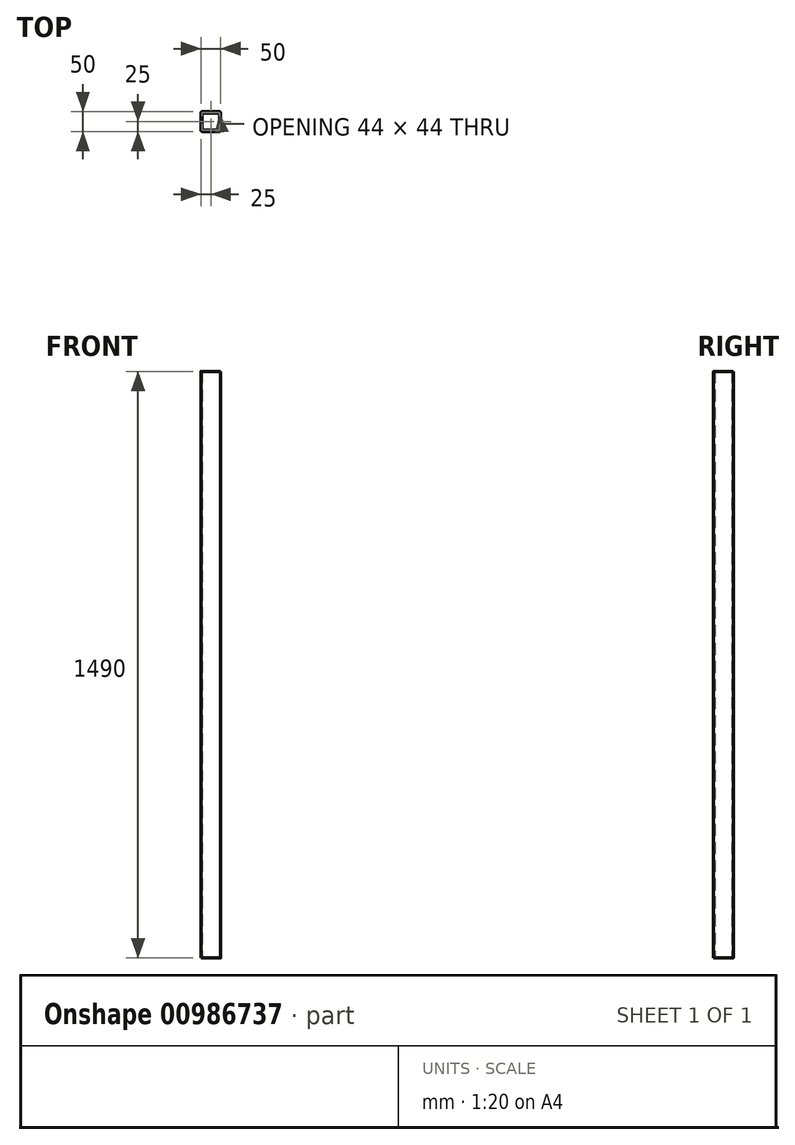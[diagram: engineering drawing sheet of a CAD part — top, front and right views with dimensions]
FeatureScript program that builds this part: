
annotation { "Feature Type Name" : "Feature", "Feature Type Description" : "" }
export const myFeature = defineFeature(function(context is Context, id is Id, definition is map)
    precondition{}
    {
        {
            var Q0;
            Q0=qCreatedBy(makeId("Top.planeOp"),FACE);
            var sketch = newSketch(context, id + "F0", { "sketchPlane" : qUnion([Q0])});
            skLineSegment(sketch, "E0.bottom", {"start": v(22, -25) * mm, "end": v(-22, -25) * mm});
            skLineSegment(sketch, "E0.top", {"start": v(22, 25) * mm, "end": v(-22, 25) * mm});
            skLineSegment(sketch, "E0.left", {"start": v(25, -22) * mm, "end": v(25, 22) * mm});
            skLineSegment(sketch, "E0.right", {"start": v(-25, -22) * mm, "end": v(-25, 22) * mm});
            skPoint(sketch, "E0.middle", {"position": v(0, 0) * mm});
            skLineSegment(sketch, "E1.0", {"start": v(-22, -19) * mm, "end": v(-22, 19) * mm});
            skLineSegment(sketch, "E1.1", {"start": v(19, -22) * mm, "end": v(-19, -22) * mm});
            skLineSegment(sketch, "E1.2", {"start": v(22, -19) * mm, "end": v(22, 19) * mm});
            skLineSegment(sketch, "E1.3", {"start": v(19, 22) * mm, "end": v(-19, 22) * mm});
            skPoint(sketch, "E2.visualSharp", {"position": v(-25, 25) * mm});
            skArc(sketch, "E2.filletArc", {"start": v(-22, 25) * mm, "mid": v(-24.12, 24.12) * mm, "end": v(-25, 22) * mm});
            skPoint(sketch, "E3.visualSharp", {"position": v(25, 25) * mm});
            skArc(sketch, "E3.filletArc", {"start": v(25, 22) * mm, "mid": v(24.12, 24.12) * mm, "end": v(22, 25) * mm});
            skPoint(sketch, "E4.visualSharp", {"position": v(25, -25) * mm});
            skArc(sketch, "E4.filletArc", {"start": v(22, -25) * mm, "mid": v(24.12, -24.12) * mm, "end": v(25, -22) * mm});
            skPoint(sketch, "E5.visualSharp", {"position": v(-25, -25) * mm});
            skArc(sketch, "E5.filletArc", {"start": v(-25, -22) * mm, "mid": v(-24.12, -24.12) * mm, "end": v(-22, -25) * mm});
            skArc(sketch, "E6.filletArc", {"start": v(22, 19) * mm, "mid": v(21.12, 21.12) * mm, "end": v(19, 22) * mm});
            skArc(sketch, "E7.filletArc", {"start": v(-19, 22) * mm, "mid": v(-21.12, 21.12) * mm, "end": v(-22, 19) * mm});
            skArc(sketch, "E8.filletArc", {"start": v(-22, -19) * mm, "mid": v(-21.12, -21.12) * mm, "end": v(-19, -22) * mm});
            skArc(sketch, "E9.filletArc", {"start": v(19, -22) * mm, "mid": v(21.12, -21.12) * mm, "end": v(22, -19) * mm});
            skSolve(sketch);
        }
        {
            var Q0;
            Q0 = qSketchRegion(id + "F0", true);
            extrude(context, id + "F1", {"entities" : qUnion([Q0]), "depth" : 1490 * mm, "offsetDistance" : 25 * mm});
        }
    });
